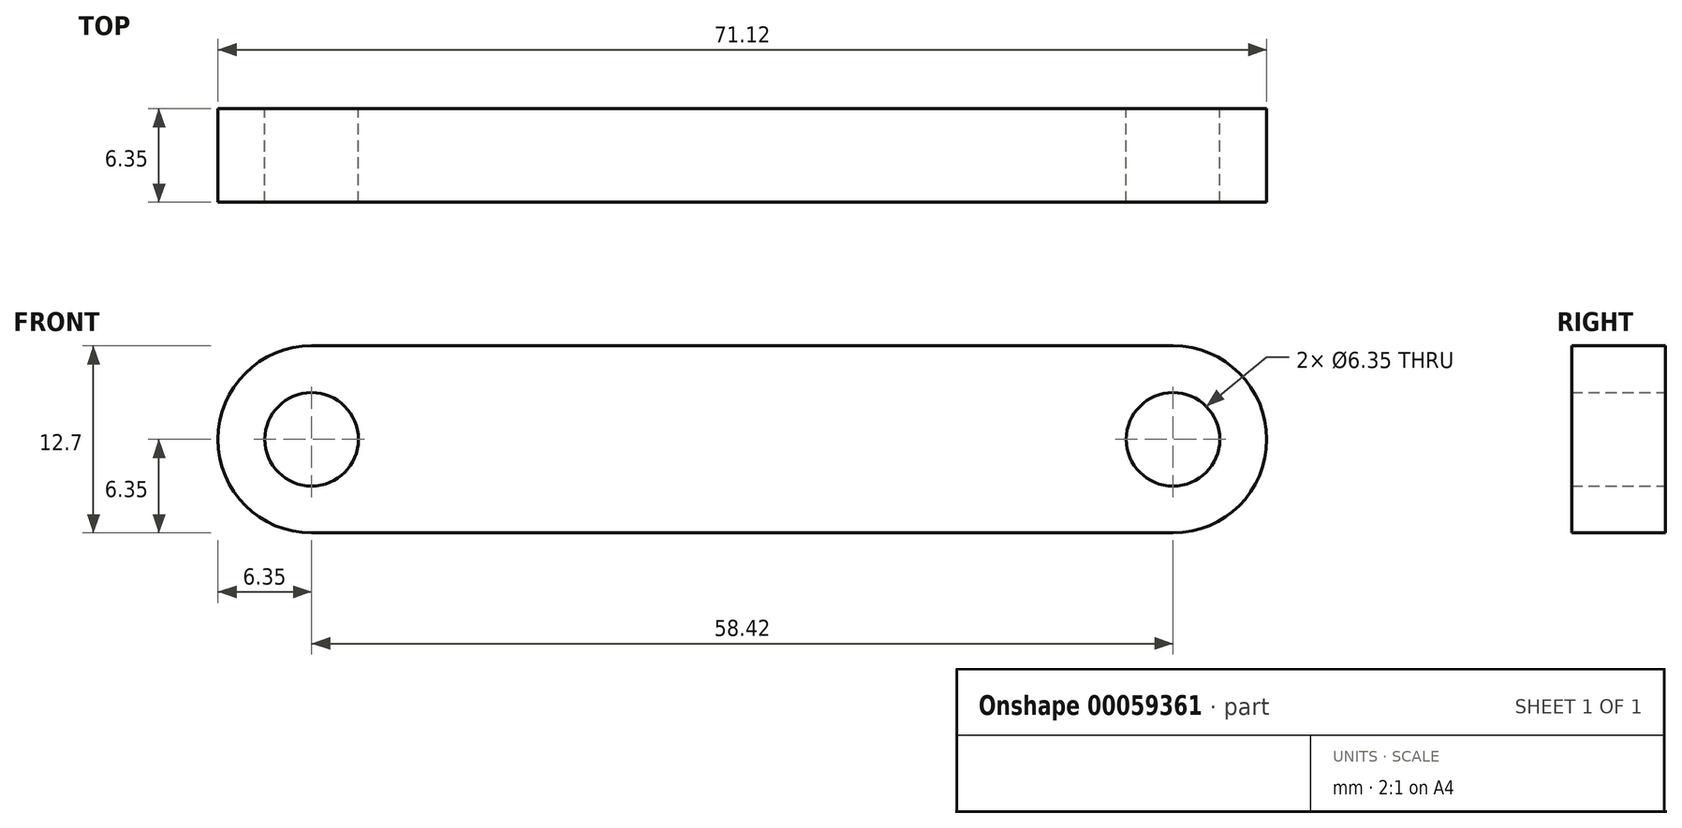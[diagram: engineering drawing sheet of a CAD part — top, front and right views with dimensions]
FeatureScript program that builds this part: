
annotation { "Feature Type Name" : "Feature", "Feature Type Description" : "" }
export const myFeature = defineFeature(function(context is Context, id is Id, definition is map)
    precondition{}
    {
        {
            var Q0;
            Q0=qCreatedBy(makeId("Front.planeOp"),FACE);
            var sketch = newSketch(context, id + "F0", { "sketchPlane" : qUnion([Q0])});
            skLineSegment(sketch, "E0", {"start": v(-44.71, 0) * mm, "end": v(44.33, 0) * mm, "construction": true});
            skLineSegment(sketch, "E1", {"start": v(0, -25.78) * mm, "end": v(0, 25.02) * mm, "construction": true});
            skArc(sketch, "E2", {"start": v(-29.33, 6.35) * mm, "mid": v(-35.68, 0) * mm, "end": v(-29.33, -6.35) * mm});
            skArc(sketch, "E3", {"start": v(29.09, -6.35) * mm, "mid": v(35.44, 0) * mm, "end": v(29.09, 6.35) * mm});
            skLineSegment(sketch, "E4", {"start": v(-29.33, 6.35) * mm, "end": v(29.09, 6.35) * mm});
            skLineSegment(sketch, "E5", {"start": v(-29.33, -6.35) * mm, "end": v(29.09, -6.35) * mm});
            skCircle(sketch, "E6", {"center": v(-29.33, 0) * mm, "radius": 3.18 * mm});
            skCircle(sketch, "E7", {"center": v(29.09, 0) * mm, "radius": 3.18 * mm});
            skSolve(sketch);
        }
        {
            var Q0;
            Q0 = qSketchRegion(id + "F0", true);
            extrude(context, id + "F1", {"entities" : qUnion([Q0]), "depth" : 6.35 * mm});
        }
    });
